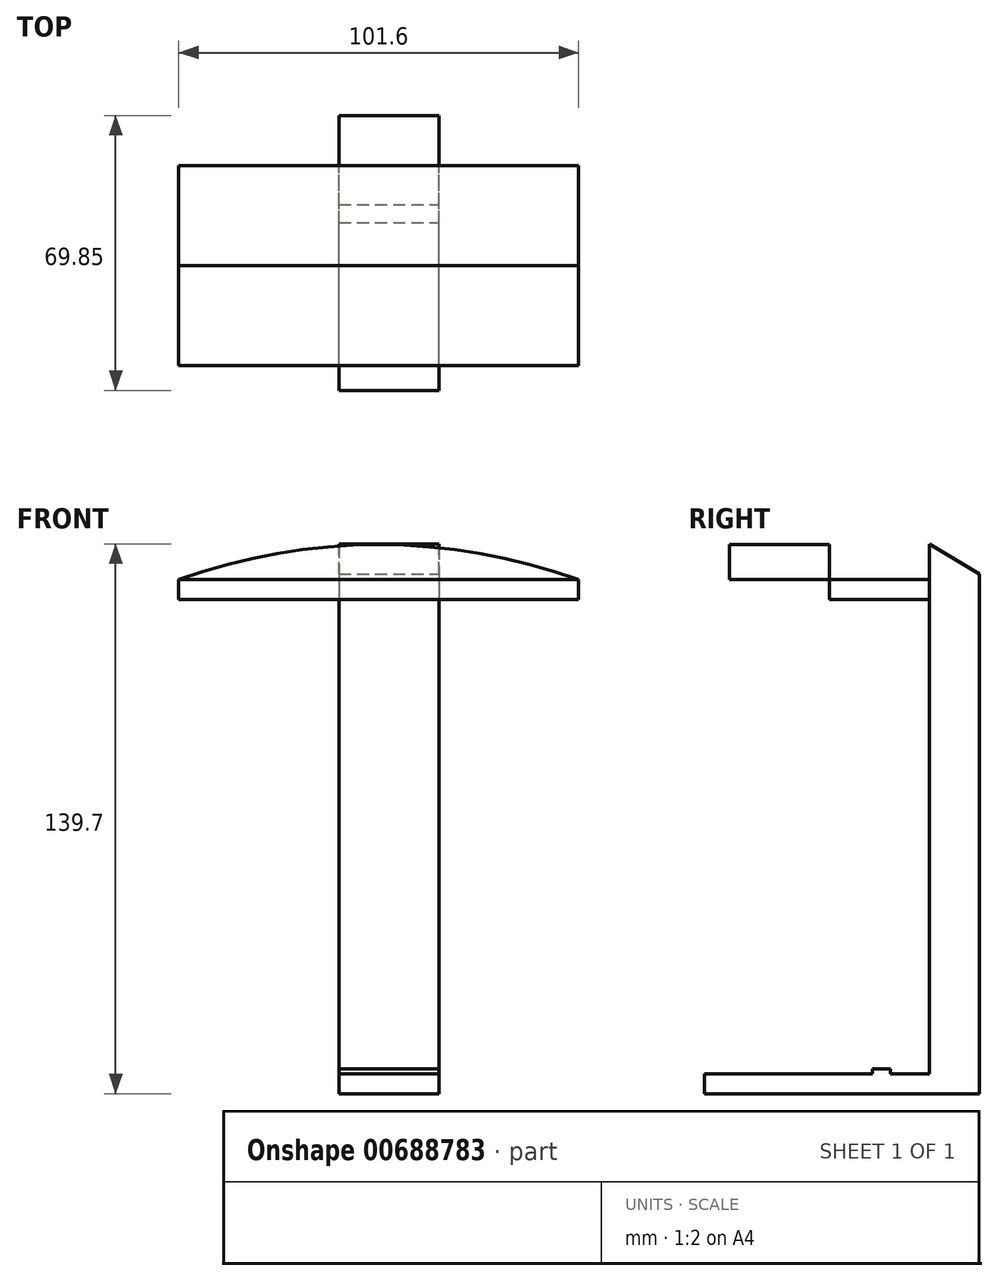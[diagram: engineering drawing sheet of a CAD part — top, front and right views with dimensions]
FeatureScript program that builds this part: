
annotation { "Feature Type Name" : "Feature", "Feature Type Description" : "" }
export const myFeature = defineFeature(function(context is Context, id is Id, definition is map)
    precondition{}
    {
        {
            var Q0;
            Q0=qCreatedBy(makeId("Front.planeOp"),FACE);
            var sketch = newSketch(context, id + "F0", { "sketchPlane" : qUnion([Q0])});
            skLineSegment(sketch, "E0.bottom", {"start": v(-57.76, 0) * mm, "end": v(-32.36, 0) * mm});
            skLineSegment(sketch, "E0.top", {"start": v(-57.76, 5.08) * mm, "end": v(-32.36, 5.08) * mm});
            skLineSegment(sketch, "E0.left", {"start": v(-57.76, 0) * mm, "end": v(-57.76, 5.08) * mm});
            skLineSegment(sketch, "E0.right", {"start": v(-32.36, 0) * mm, "end": v(-32.36, 5.08) * mm});
            skLineSegment(sketch, "E1.bottom", {"start": v(-57.76, 132.08) * mm, "end": v(-32.36, 132.08) * mm});
            skLineSegment(sketch, "E1.left", {"start": v(-57.76, 132.08) * mm, "end": v(-57.76, 5.08) * mm});
            skLineSegment(sketch, "E1.right", {"start": v(-32.36, 132.08) * mm, "end": v(-32.36, 5.08) * mm});
            skSolve(sketch);
        }
        {
            var Q0;
            Q0=makeQuery(id+"F0.imprint","IMPRINT",FACE,{"disambiguationData":[TD([[makeQuery(id+"F0.imprint","IMPRINT",EDGE,{"derivedFrom":sQuery(id+"F0.wireOp",EDGE,"E1.bottom")}),-1.0]])]});
            extrude(context, id + "F1", {"entities" : qUnion([Q0]), "depth" : 12.7 * mm, "offsetDistance" : 25.4 * mm});
        }
        {
            var Q0;
            Q0=makeQuery(id+"F1.opExtrude","CAP_FACE",FACE,{"disambiguationData":[OSD([sQuery(id+"F0.wireOp",EDGE,"E1.bottom"),sQuery(id+"F0.wireOp",EDGE,"E0.top"),sQuery(id+"F0.wireOp",EDGE,"E1.left"),sQuery(id+"F0.wireOp",EDGE,"E1.right")])],"isStart":true});
            var sketch = newSketch(context, id + "F2", { "sketchPlane" : qUnion([Q0])});
            skLineSegment(sketch, "E2.bottom", {"start": v(32.36, 5.08) * mm, "end": v(57.76, 5.08) * mm});
            skLineSegment(sketch, "E2.top", {"start": v(32.36, 0) * mm, "end": v(57.76, 0) * mm});
            skLineSegment(sketch, "E2.left", {"start": v(32.36, 5.08) * mm, "end": v(32.36, 0) * mm});
            skLineSegment(sketch, "E2.right", {"start": v(57.76, 5.08) * mm, "end": v(57.76, 0) * mm});
            skSolve(sketch);
        }
        {
            var Q0;
            Q0=makeQuery(id+"F2.imprint","IMPRINT",FACE,{"disambiguationData":[TD([[makeQuery(id+"F2.imprint","IMPRINT",EDGE,{"derivedFrom":sQuery(id+"F2.wireOp",EDGE,"E2.bottom")}),1.0]])]});
            extrude(context, id + "F3", {"entities" : qUnion([Q0]), "operationType" : NewBodyOperationType.ADD, "oppositeDirection" : true, "depth" : 69.85 * mm, "offsetDistance" : 25.4 * mm});
        }
        {
            var Q0;
            Q0=makeQuery(id+"F3.boolean.opBoolean","MERGE",FACE,{"derivedFrom":[makeQuery(id+"F1.opExtrude","SWEPT_FACE",FACE,{"disambiguationData":[OSD([sQuery(id+"F0.wireOp",EDGE,"E1.right")])]}),makeQuery(id+"F3.opExtrude","SWEPT_FACE",FACE,{"disambiguationData":[OSD([sQuery(id+"F2.wireOp",EDGE,"E2.left")])]})]});
            var sketch = newSketch(context, id + "F4", { "sketchPlane" : qUnion([Q0])});
            skLineSegment(sketch, "E3", {"start": v(-12.7, 139.7) * mm, "end": v(-12.7, 132.08) * mm});
            skLineSegment(sketch, "E4", {"start": v(-12.7, 132.08) * mm, "end": v(0, 132.08) * mm});
            skLineSegment(sketch, "E5", {"start": v(0, 132.08) * mm, "end": v(-12.7, 139.7) * mm});
            skSolve(sketch);
        }
        {
            var Q0;
            Q0=makeQuery(id+"F4.imprint","IMPRINT",FACE,{"disambiguationData":[TD([[makeQuery(id+"F4.imprint","IMPRINT",EDGE,{"derivedFrom":sQuery(id+"F4.wireOp",EDGE,"E3")}),1.0]])]});
            extrude(context, id + "F5", {"entities" : qUnion([Q0]), "operationType" : NewBodyOperationType.ADD, "oppositeDirection" : true, "depth" : 25.4 * mm, "offsetDistance" : 25.4 * mm});
        }
        {
            var Q0;
            Q0=makeQuery(id+"F5.boolean.opBoolean","MERGE",FACE,{"derivedFrom":[makeQuery(id+"F1.opExtrude","CAP_FACE",FACE,{"disambiguationData":[OSD([sQuery(id+"F0.wireOp",EDGE,"E1.bottom"),sQuery(id+"F0.wireOp",EDGE,"E0.top"),sQuery(id+"F0.wireOp",EDGE,"E1.left"),sQuery(id+"F0.wireOp",EDGE,"E1.right")])],"isStart":false}),makeQuery(id+"F5.opExtrude","SWEPT_FACE",FACE,{"disambiguationData":[OSD([sQuery(id+"F4.wireOp",EDGE,"E3")])]})]});
            var sketch = newSketch(context, id + "F6", { "sketchPlane" : qUnion([Q0])});
            skLineSegment(sketch, "E6", {"start": v(-98.5, 130.62) * mm, "end": v(-98.5, 125.54) * mm});
            skLineSegment(sketch, "E7", {"start": v(-98.5, 125.54) * mm, "end": v(3.1, 125.54) * mm});
            skLineSegment(sketch, "E8", {"start": v(3.1, 125.54) * mm, "end": v(3.1, 130.62) * mm});
            skLineSegment(sketch, "E9", {"start": v(3.1, 130.62) * mm, "end": v(-98.5, 130.62) * mm});
            skSolve(sketch);
        }
        {
            var Q0;
            {var subQ0=sQuery(id+"F6.wireOp",EDGE,"E6");Q0=makeQuery(id+"F6.imprint","IMPRINT",FACE,{"disambiguationData":[TD([[makeQuery(id+"F6.imprint","IMPRINT",EDGE,{"derivedFrom":subQ0}),1.0]])]});}
            var Q1;
            {var subQ0=sQuery(id+"F6.wireOp",EDGE,"E8");Q1=makeQuery(id+"F6.imprint","IMPRINT",FACE,{"disambiguationData":[TD([[makeQuery(id+"F6.imprint","IMPRINT",EDGE,{"derivedFrom":subQ0}),1.0]])]});}
            var Q2;
            {var subQ0=sQuery(id+"F6.wireOp",EDGE,"E7");var subQ1=sQuery(id+"F4.wireOp",EDGE,"E3");var subQ2=makeQuery(id+"F5.boolean.opBoolean","MERGE",EDGE,{"derivedFrom":[makeQuery(id+"F1.opExtrude","CAP_EDGE",EDGE,{"disambiguationData":[OSD([sQuery(id+"F0.wireOp",EDGE,"E1.left")])],"isStart":false}),makeQuery(id+"F5.opExtrude","CAP_EDGE",EDGE,{"disambiguationData":[OSD([subQ1])],"isStart":false})]});var subQ3=makeQuery(id+"F6.imprint","INTERSECT",VERTEX,{"derivedFrom":[subQ2,subQ0]});Q2=makeQuery(id+"F6.imprint","IMPRINT",FACE,{"disambiguationData":[TD([[makeQuery(id+"F6.imprint","IMPRINT",EDGE,{"disambiguationData":[TD([[subQ3,-1.0]])],"derivedFrom":subQ0}),1.0]])]});}
            extrude(context, id + "F7", {"entities" : qUnion([Q0, Q1, Q2]), "operationType" : NewBodyOperationType.ADD, "depth" : 25.4 * mm, "offsetDistance" : 25.4 * mm});
        }
        {
            var Q0;
            Q0=makeQuery(id+"F7.opExtrude","CAP_FACE",FACE,{"disambiguationData":[OSD([sQuery(id+"F6.wireOp",EDGE,"E6"),sQuery(id+"F6.wireOp",EDGE,"E7"),sQuery(id+"F6.wireOp",EDGE,"E8"),sQuery(id+"F6.wireOp",EDGE,"E9")])],"isStart":false});
            var sketch = newSketch(context, id + "F8", { "sketchPlane" : qUnion([Q0])});
            skArc(sketch, "E10", {"start": v(3.1, 130.62) * mm, "mid": v(-47.7, 139.47) * mm, "end": v(-98.5, 130.62) * mm});
            skSolve(sketch);
        }
        {
            var Q0;
            Q0=makeQuery(id+"F8.imprint","IMPRINT",FACE,{"disambiguationData":[TD([[makeQuery(id+"F8.imprint","IMPRINT",EDGE,{"derivedFrom":sQuery(id+"F8.wireOp",EDGE,"E10")}),1.0]])]});
            extrude(context, id + "F9", {"entities" : qUnion([Q0]), "depth" : 25.4 * mm, "offsetDistance" : 25.4 * mm});
        }
        {
            var Q0;
            Q0=makeQuery(id+"F3.opExtrude","SWEPT_FACE",FACE,{"disambiguationData":[OSD([sQuery(id+"F2.wireOp",EDGE,"E2.bottom")])]});
            var sketch = newSketch(context, id + "F10", { "sketchPlane" : qUnion([Q0])});
            skLineSegment(sketch, "E11.bottom", {"start": v(-57.76, -22.63) * mm, "end": v(-32.36, -22.63) * mm});
            skLineSegment(sketch, "E11.top", {"start": v(-57.76, -27.18) * mm, "end": v(-32.36, -27.18) * mm});
            skLineSegment(sketch, "E11.left", {"start": v(-57.76, -22.63) * mm, "end": v(-57.76, -27.18) * mm});
            skLineSegment(sketch, "E11.right", {"start": v(-32.36, -22.63) * mm, "end": v(-32.36, -27.18) * mm});
            skSolve(sketch);
        }
        {
            var Q0;
            Q0=makeQuery(id+"F10.imprint","IMPRINT",FACE,{"disambiguationData":[TD([[makeQuery(id+"F10.imprint","IMPRINT",EDGE,{"derivedFrom":sQuery(id+"F10.wireOp",EDGE,"E11.bottom")}),-1.0]])]});
            extrude(context, id + "F11", {"entities" : qUnion([Q0]), "operationType" : NewBodyOperationType.ADD, "depth" : 1.27 * mm, "offsetDistance" : 25.4 * mm});
        }
    });
